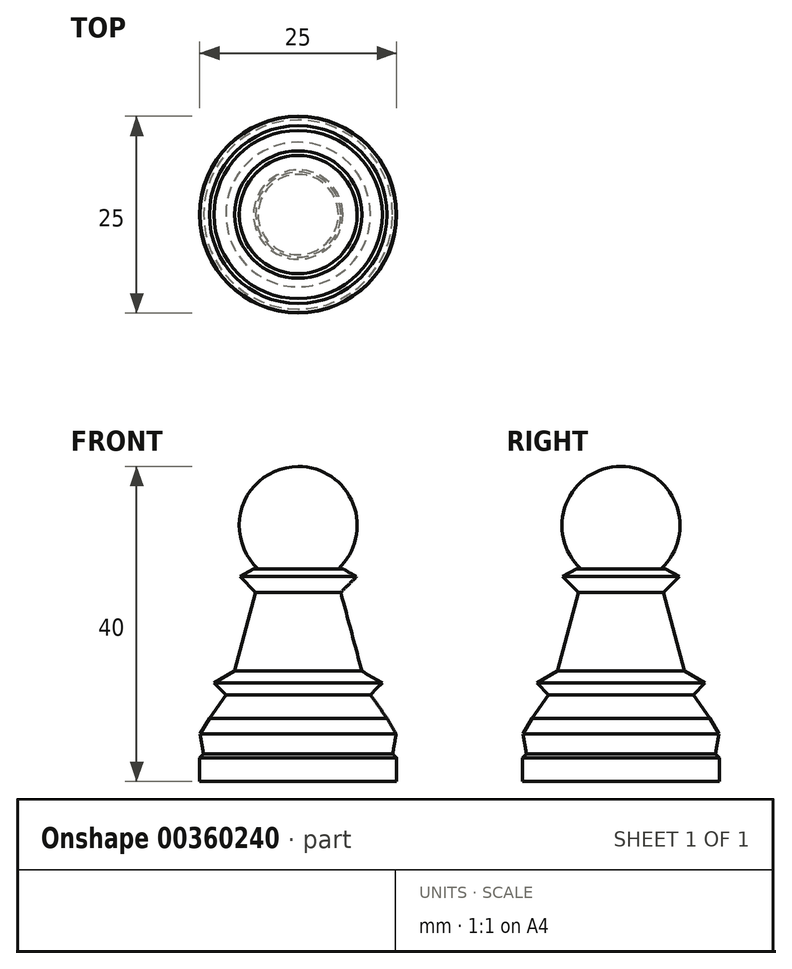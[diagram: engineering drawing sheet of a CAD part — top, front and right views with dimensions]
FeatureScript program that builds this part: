
annotation { "Feature Type Name" : "Feature", "Feature Type Description" : "" }
export const myFeature = defineFeature(function(context is Context, id is Id, definition is map)
    precondition{}
    {
        {
            var Q0;
            Q0=qCreatedBy(makeId("Top.planeOp"),FACE);
            var sketch = newSketch(context, id + "F0", { "sketchPlane" : qUnion([Q0])});
            skCircle(sketch, "E0", {"center": v(0, 0) * mm, "radius": 12.5 * mm});
            skSolve(sketch);
        }
        {
            var Q0;
            Q0 = qSketchRegion(id + "F0", true);
            extrude(context, id + "F1", {"entities" : qUnion([Q0]), "depth" : 3 * mm});
        }
        {
            var Q0;
            Q0=makeQuery(id+"F1.opExtrude","CAP_FACE",FACE,{"disambiguationData":[OSD([sQuery(id+"F0.wireOp",EDGE,"E0")])],"isStart":false});
            extrude(context, id + "F2", {"entities" : qUnion([Q0]), "operationType" : NewBodyOperationType.ADD, "depth" : .5 * mm, "hasDraft" : true, "draftAngle" : 45 * degree, "draftPullDirection" : true});
        }
        {
            var Q0;
            Q0=makeQuery(id+"F2.opExtrude","CAP_FACE",FACE,{"disambiguationData":[OSD([sQuery(id+"F0.wireOp",EDGE,"E0")])],"isStart":false});
            extrude(context, id + "F3", {"entities" : qUnion([Q0]), "operationType" : NewBodyOperationType.ADD, "depth" : 2.5 * mm, "hasDraft" : true, "draftAngle" : 10 * degree});
        }
        {
            var Q0;
            Q0=makeQuery(id+"F3.opExtrude","CAP_FACE",FACE,{"disambiguationData":[OSD([sQuery(id+"F0.wireOp",EDGE,"E0")])],"isStart":false});
            extrude(context, id + "F4", {"entities" : qUnion([Q0]), "operationType" : NewBodyOperationType.ADD, "depth" : 2 * mm, "hasDraft" : true, "draftAngle" : 30 * degree, "draftPullDirection" : true});
        }
        {
            var Q0;
            Q0=makeQuery(id+"F4.opExtrude","CAP_FACE",FACE,{"disambiguationData":[OSD([sQuery(id+"F0.wireOp",EDGE,"E0")])],"isStart":false});
            extrude(context, id + "F5", {"entities" : qUnion([Q0]), "operationType" : NewBodyOperationType.ADD, "depth" : 3 * mm, "hasDraft" : true, "draftAngle" : 35 * degree, "draftPullDirection" : true});
        }
        {
            var Q0;
            Q0=makeQuery(id+"F5.opExtrude","CAP_FACE",FACE,{"disambiguationData":[OSD([sQuery(id+"F0.wireOp",EDGE,"E0")])],"isStart":false});
            extrude(context, id + "F6", {"entities" : qUnion([Q0]), "operationType" : NewBodyOperationType.ADD, "depth" : 1.5 * mm, "hasDraft" : true, "draftAngle" : 45 * degree});
        }
        {
            var Q0;
            Q0=makeQuery(id+"F6.opExtrude","CAP_FACE",FACE,{"disambiguationData":[OSD([sQuery(id+"F0.wireOp",EDGE,"E0")])],"isStart":false});
            extrude(context, id + "F7", {"entities" : qUnion([Q0]), "operationType" : NewBodyOperationType.ADD, "depth" : 1.5 * mm, "hasDraft" : true, "draftAngle" : 60 * degree, "draftPullDirection" : true});
        }
        {
            var Q0;
            Q0=makeQuery(id+"F7.opExtrude","CAP_FACE",FACE,{"disambiguationData":[OSD([sQuery(id+"F0.wireOp",EDGE,"E0")])],"isStart":false});
            extrude(context, id + "F8", {"entities" : qUnion([Q0]), "operationType" : NewBodyOperationType.ADD, "depth" : 10 * mm, "hasDraft" : true, "draftAngle" : 15 * degree, "draftPullDirection" : true});
        }
        {
            var Q0;
            Q0=makeQuery(id+"F8.opExtrude","CAP_FACE",FACE,{"disambiguationData":[OSD([sQuery(id+"F0.wireOp",EDGE,"E0")])],"isStart":false});
            extrude(context, id + "F9", {"entities" : qUnion([Q0]), "operationType" : NewBodyOperationType.ADD, "depth" : 2 * mm, "hasDraft" : true, "draftAngle" : 45 * degree});
        }
        {
            var Q0;
            Q0=makeQuery(id+"F9.opExtrude","CAP_FACE",FACE,{"disambiguationData":[OSD([sQuery(id+"F0.wireOp",EDGE,"E0")])],"isStart":false});
            extrude(context, id + "F10", {"entities" : qUnion([Q0]), "operationType" : NewBodyOperationType.ADD, "depth" : 1 * mm, "hasDraft" : true, "draftAngle" : 60 * degree, "draftPullDirection" : true});
        }
        {
            var Q0;
            Q0=qCreatedBy(makeId("Front.planeOp"),FACE);
            var sketch = newSketch(context, id + "F11", { "sketchPlane" : qUnion([Q0])});
            skLineSegment(sketch, "E1", {"start": v(0, 0) * mm, "end": v(0, 32.5) * mm});
            skCircle(sketch, "E2", {"center": v(0, 32.5) * mm, "radius": 7.5 * mm});
            skLineSegment(sketch, "E3", {"start": v(0, 32.5) * mm, "end": v(0, 53.32) * mm});
            skSolve(sketch);
        }
        {
            var Q0;
            {var subQ0=sQuery(id+"F11.wireOp",EDGE,"E3");var subQ1=sQuery(id+"F11.wireOp",EDGE,"E1");var subQ2=makeQuery(id+"F11.imprint","INTERSECT",VERTEX,{"derivedFrom":[subQ1,subQ0]});Q0=makeQuery(id+"F11.imprint","IMPRINT",FACE,{"disambiguationData":[TD([[makeQuery(id+"F11.imprint","IMPRINT",EDGE,{"disambiguationData":[TD([[subQ2,1.0]])],"derivedFrom":subQ1}),-1.0]])]});}
            var Q1;
            Q1=sQuery(id+"F11.wireOp",EDGE,"E3");
            revolve(context, id + "F12", {"operationType" : NewBodyOperationType.ADD, "entities" : qUnion([Q0]), "axis" : qUnion([Q1]), "revolveType" : RevolveType.FULL});
        }
    });
